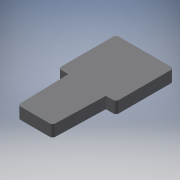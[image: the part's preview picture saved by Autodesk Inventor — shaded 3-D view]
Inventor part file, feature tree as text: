
AUTODESK INVENTOR PART (.ipt)
format: ipt  version: 2018 (Build 220112000, 112)  size: 144,896 bytes
history: native  units: mm
features: other x2, sheet_metal_op x1, sketch x1
ambient origin geometry x8: Origin, YZ Plane, XZ Plane, XY Plane, X Axis, Y Axis, Z Axis, Center Point
bodies: Solid1 (feature_tree)
feature tree (4):
  sheet_metal_op  "Face1"
  sketch  "Sketch1"  dims[d0=24.0mm d1=26.0mm d2=40.0mm d3=36.0mm d4=40.0mm d5=2.0mm d6=8.0mm]
  other  "Plate1"
  other  "Definition1"
